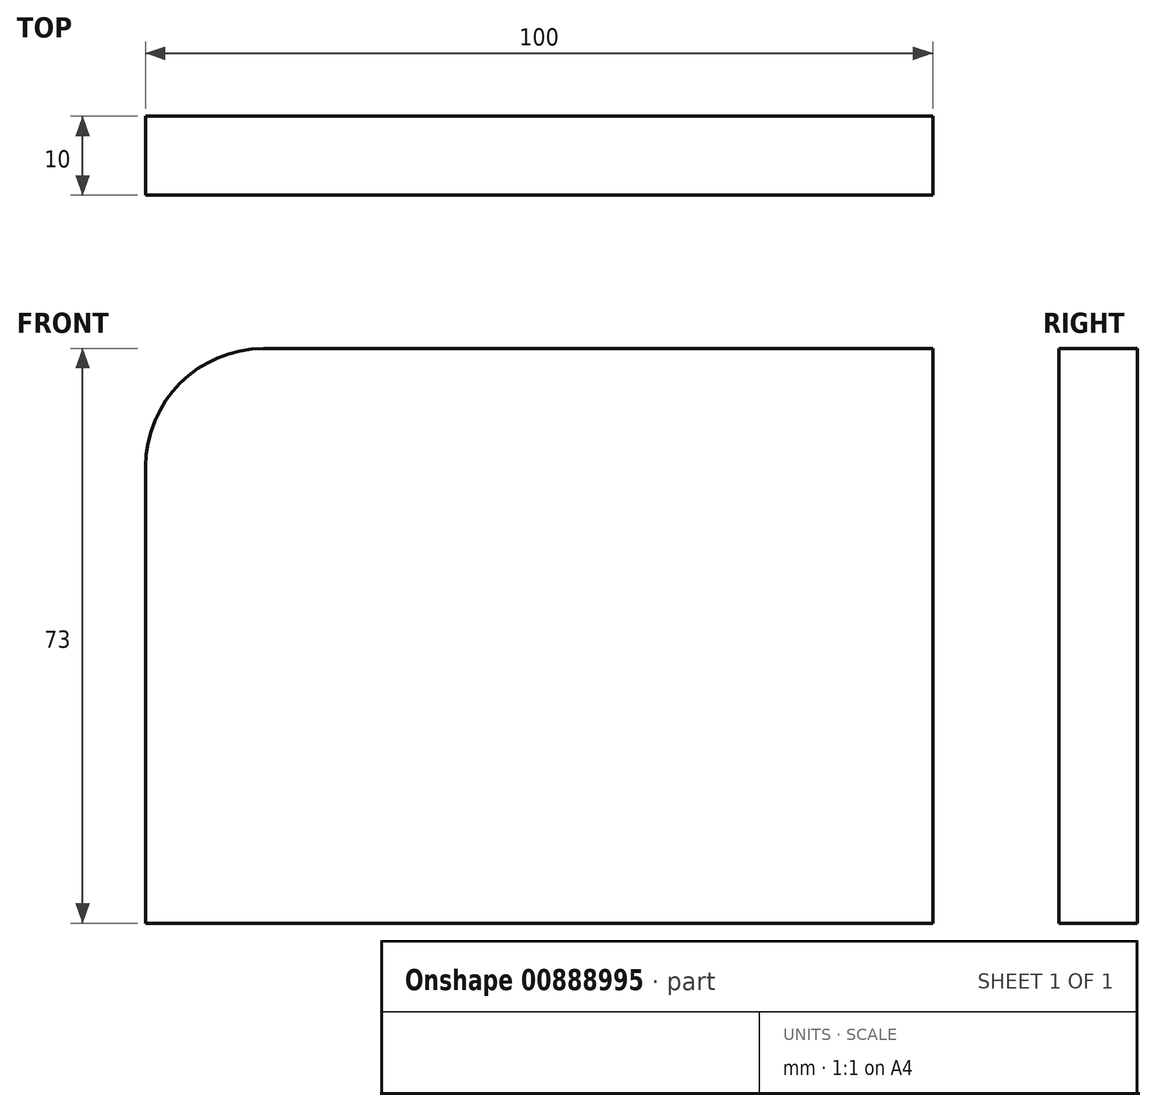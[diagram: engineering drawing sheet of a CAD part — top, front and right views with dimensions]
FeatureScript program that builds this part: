
annotation { "Feature Type Name" : "Feature", "Feature Type Description" : "" }
export const myFeature = defineFeature(function(context is Context, id is Id, definition is map)
    precondition{}
    {
        {
            var Q0;
            Q0=qCreatedBy(makeId("Front.planeOp"),FACE);
            var sketch = newSketch(context, id + "F0", { "sketchPlane" : qUnion([Q0])});
            skLineSegment(sketch, "E0.bottom", {"start": v(-41.8, 48.24) * mm, "end": v(43.2, 48.24) * mm});
            skLineSegment(sketch, "E0.top", {"start": v(-56.8, -24.76) * mm, "end": v(43.2, -24.76) * mm});
            skLineSegment(sketch, "E0.left", {"start": v(-56.8, 33.24) * mm, "end": v(-56.8, -24.76) * mm});
            skLineSegment(sketch, "E0.right", {"start": v(43.2, 48.24) * mm, "end": v(43.2, -24.76) * mm});
            skPoint(sketch, "E1.visualSharp", {"position": v(-56.8, 48.24) * mm});
            skArc(sketch, "E1.filletArc", {"start": v(-41.8, 48.24) * mm, "mid": v(-52.4, 43.84) * mm, "end": v(-56.8, 33.24) * mm});
            skSolve(sketch);
        }
        {
            var Q0;
            Q0=makeQuery(id+"F0.imprint","IMPRINT",FACE,{"disambiguationData":[TD([[makeQuery(id+"F0.imprint","IMPRINT",EDGE,{"derivedFrom":sQuery(id+"F0.wireOp",EDGE,"E0.bottom")}),-1.0]])]});
            extrude(context, id + "F1", {"entities" : qUnion([Q0]), "depth" : 10 * mm, "offsetDistance" : 25 * mm});
        }
    });
